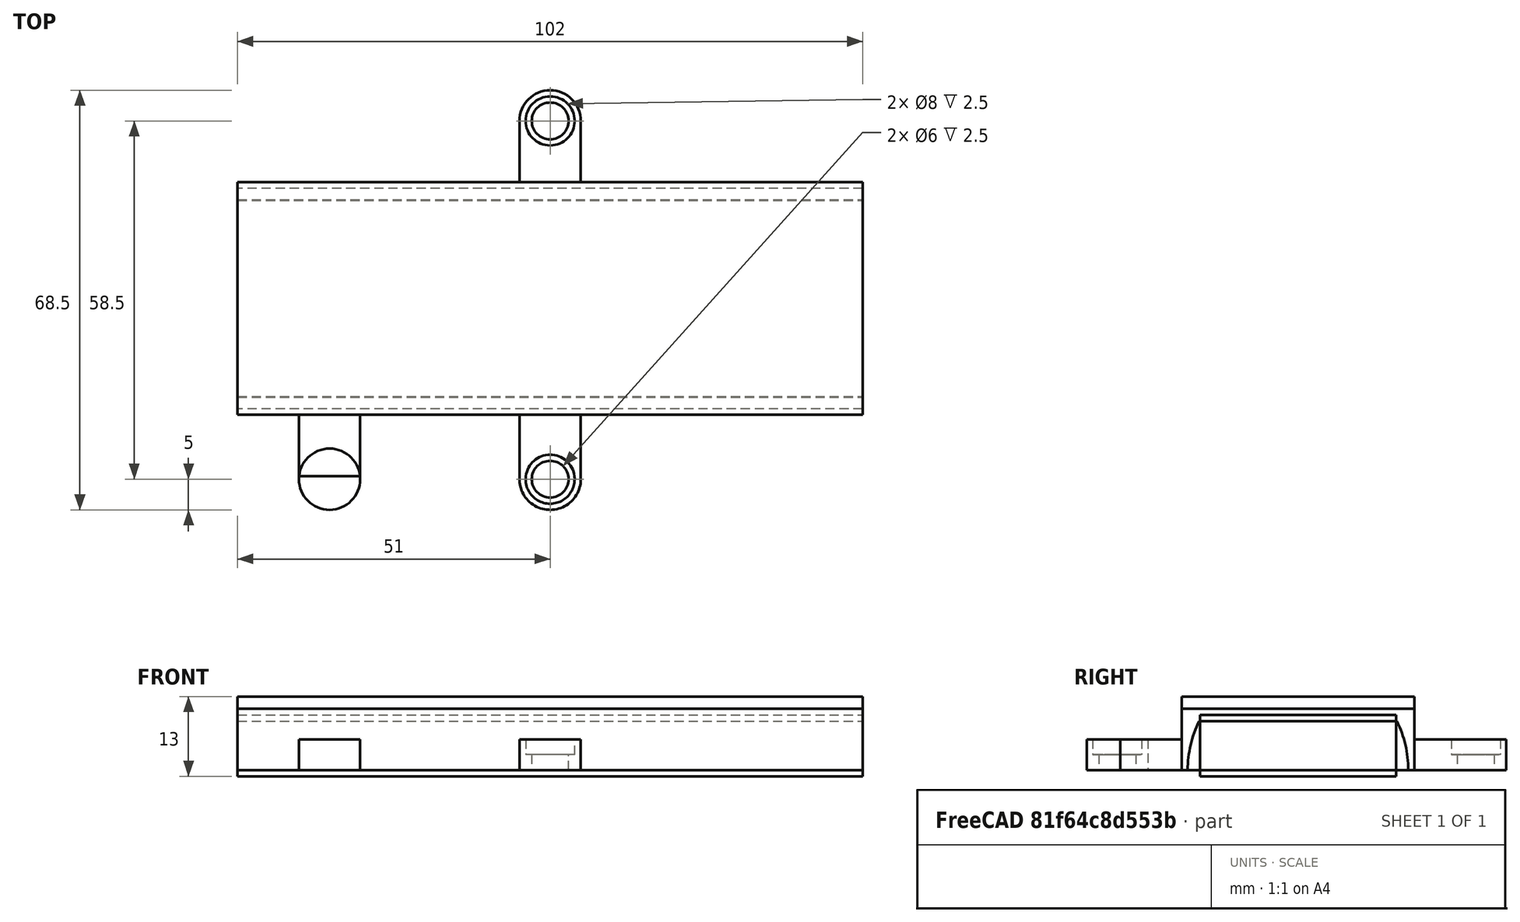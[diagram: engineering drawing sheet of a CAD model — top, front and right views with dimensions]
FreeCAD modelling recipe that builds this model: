
FCSTD DOCUMENT  (FreeCAD 1.0RUnknown)
Label: cable-management-v2
License: All rights reserved
LicenseURL: https://en.wikipedia.org/wiki/All_rights_reserved
objects: Part::Cylinder×8, Part::Box×7, Part::Cut×6, Part::MultiFuse×2
note: 23 computed .brp shape members not serialized (recipe doc carries the construction recipe); baked Part::Feature solids carry a one-line shape summary decoded from their .brp

FEATURE [Part::Box] Box  label="Cube"
  AttacherType = Attacher::AttachEngine3D
  Height = 10
  Length = 102
  Width = 38
FEATURE [Part::Box] Box001  label="Cube001"
  AttacherType = Attacher::AttachEngine3D
  Height = 5
  Length = 10
  Placement = pos=(46,-10,0) rot=(0,0,1;0rad)
  Width = 10
FEATURE [Part::Cylinder] Cylinder001
  Angle = 360
  AttacherType = Attacher::AttachEngine3D
  FirstAngle = 0
  Height = 5
  Placement = pos=(51,-10.5,0) rot=(0,0,1;0rad)
  Radius = 5
  SecondAngle = 0
FEATURE [Part::Cylinder] Cylinder003
  Angle = 180
  AttacherType = Attacher::AttachEngine3D
  FirstAngle = 0
  Height = 102
  Placement = pos=(102,19,0) rot=(0.58,-0.58,-0.58;2.0944rad)
  Radius = 18
  SecondAngle = 0
FEATURE [Part::Box] Box002  label="Cube002"
  AttacherType = Attacher::AttachEngine3D
  Height = 10
  Length = 102
  Placement = pos=(0,0,8) rot=(0,0,1;0rad)
  Width = 38
FEATURE [Part::Cut] Cut002
  Base = -> Cylinder003
  Tool = -> Box002
FEATURE [Part::Cut] Cut003
  Base = -> Box
  Tool = -> Cut002
FEATURE [Part::Box] Box003  label="Cube003"
  AttacherType = Attacher::AttachEngine3D
  Height = 5
  Length = 10
  Placement = pos=(46,38,0) rot=(0,0,1;0rad)
  Width = 10
FEATURE [Part::Cylinder] Cylinder004
  Angle = 360
  AttacherType = Attacher::AttachEngine3D
  FirstAngle = 0
  Height = 5
  Placement = pos=(51,48,0) rot=(0,0,1;0rad)
  Radius = 5
  SecondAngle = 0
FEATURE [Part::Box] Box004  label="Cube004"
  AttacherType = Attacher::AttachEngine3D
  Height = 5
  Length = 10
  Placement = pos=(10,-10,0) rot=(0,0,1;0rad)
  Width = 10
FEATURE [Part::Cylinder] Cylinder005
  Angle = 360
  AttacherType = Attacher::AttachEngine3D
  FirstAngle = 0
  Height = 5
  Placement = pos=(15,-10.5,0) rot=(0,0,1;0rad)
  Radius = 5
  SecondAngle = 0
FEATURE [Part::Cylinder] Cylinder006
  Angle = 360
  AttacherType = Attacher::AttachEngine3D
  FirstAngle = 0
  Height = 5
  Placement = pos=(51,-10.5,2.5) rot=(0,0,1;0rad)
  Radius = 4
  SecondAngle = 0
FEATURE [Part::Cylinder] Cylinder007
  Angle = 360
  AttacherType = Attacher::AttachEngine3D
  FirstAngle = 0
  Height = 5
  Placement = pos=(51,48,2.5) rot=(0,0,1;0rad)
  Radius = 4
  SecondAngle = 0
FEATURE [Part::MultiFuse] Fusion
  Shapes = -> [Box001,Cylinder001]
FEATURE [Part::MultiFuse] Fusion001
  Shapes = -> [Box003,Cylinder004]
FEATURE [Part::Cylinder] Cylinder008
  Angle = 360
  AttacherType = Attacher::AttachEngine3D
  FirstAngle = 0
  Height = 5
  Placement = pos=(51,-10.5,-0.5) rot=(0,0,1;0rad)
  Radius = 3
  SecondAngle = 0
FEATURE [Part::Cylinder] Cylinder009
  Angle = 360
  AttacherType = Attacher::AttachEngine3D
  FirstAngle = 0
  Height = 5
  Placement = pos=(51,48,-0.5) rot=(0,0,1;0rad)
  Radius = 3
  SecondAngle = 0
FEATURE [Part::Cut] Cut
  Base = -> Fusion
  Tool = -> Cylinder006
FEATURE [Part::Cut] Cut004
  Base = -> Fusion001
  Tool = -> Cylinder007
FEATURE [Part::Cut] Cut005
  Base = -> Cut
  Tool = -> Cylinder008
FEATURE [Part::Cut] Cut006
  Base = -> Cut004
  Tool = -> Cylinder009
FEATURE [Part::Box] Box005  label="Cube005"
  AttacherType = Attacher::AttachEngine3D
  Height = 12
  Length = 102
  Width = 38
FEATURE [Part::Box] Box006  label="Cube006"
  AttacherType = Attacher::AttachEngine3D
  Height = 10
  Length = 102
  Placement = pos=(0,3,-1) rot=(0,0,1;0rad)
  Width = 32
